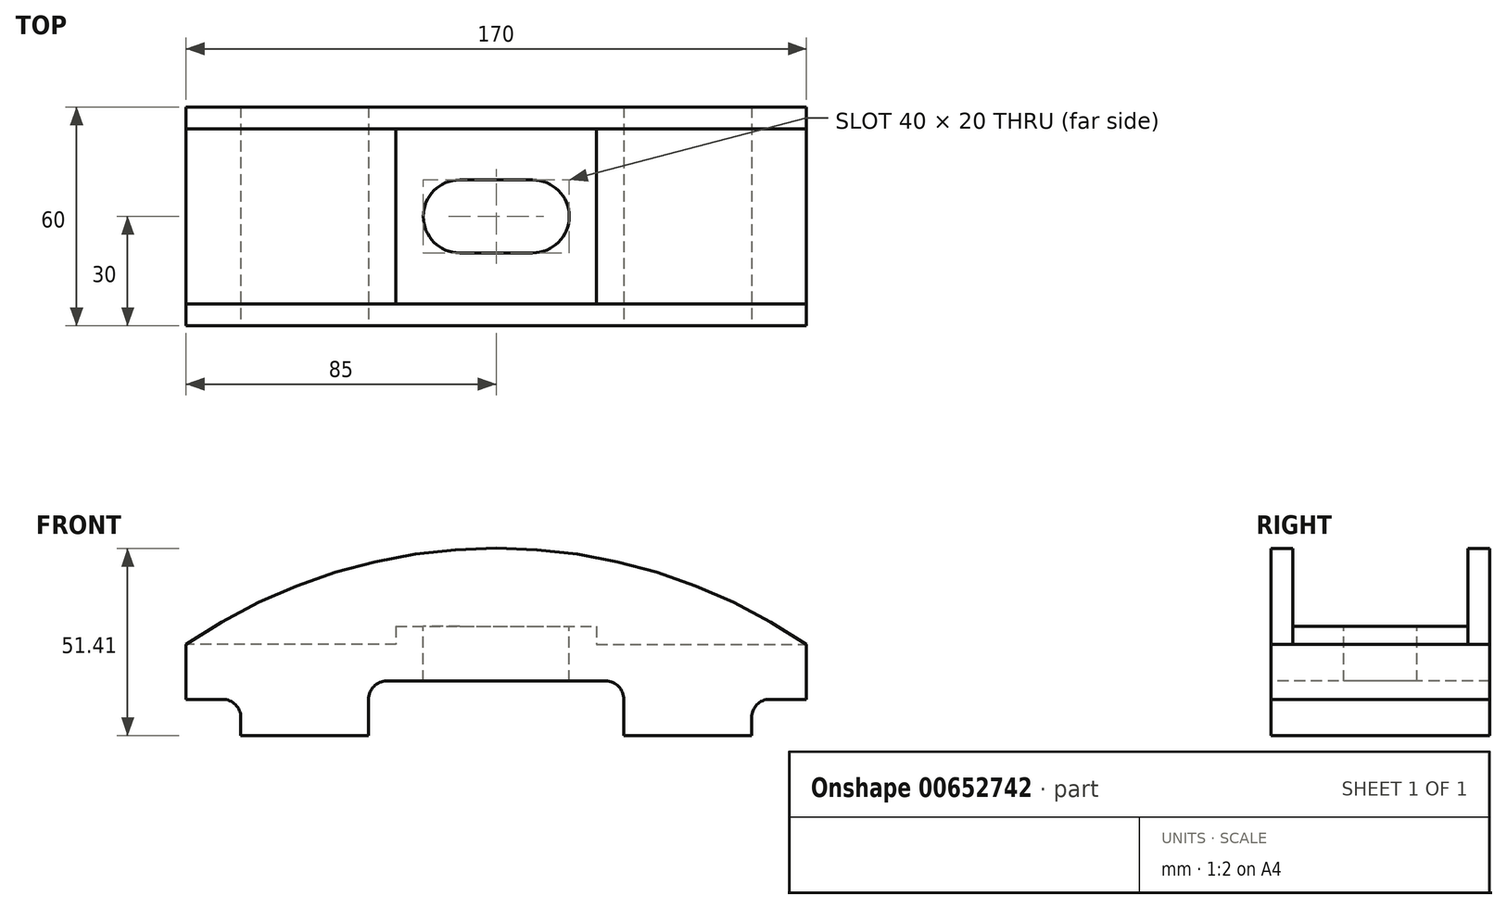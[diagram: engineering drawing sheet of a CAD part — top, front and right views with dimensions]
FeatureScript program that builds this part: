
annotation { "Feature Type Name" : "Feature", "Feature Type Description" : "" }
export const myFeature = defineFeature(function(context is Context, id is Id, definition is map)
    precondition{}
    {
        {
            var Q0;
            Q0=qCreatedBy(makeId("Front.planeOp"),FACE);
            var sketch = newSketch(context, id + "F0", { "sketchPlane" : qUnion([Q0])});
            skLineSegment(sketch, "E0.bottom", {"start": v(-85, 15) * mm, "end": v(85, 15) * mm});
            skLineSegment(sketch, "E0.top", {"start": v(-85, -15) * mm, "end": v(85, -15) * mm});
            skLineSegment(sketch, "E0.left", {"start": v(-85, 15) * mm, "end": v(-85, -15) * mm});
            skLineSegment(sketch, "E0.right", {"start": v(85, 15) * mm, "end": v(85, -15) * mm});
            skPoint(sketch, "E0.middle", {"position": v(0, 0) * mm});
            skSolve(sketch);
        }
        {
            var Q0;
            Q0 = qSketchRegion(id + "F0", true);
            extrude(context, id + "F1", {"entities" : qUnion([Q0]), "depth" : 60 * mm, "offsetDistance" : 25 * mm});
        }
        {
            var Q0;
            Q0=makeQuery(id+"F1.opExtrude","CAP_FACE",FACE,{"disambiguationData":[OSD([sQuery(id+"F0.wireOp",EDGE,"E0.bottom"),sQuery(id+"F0.wireOp",EDGE,"E0.top"),sQuery(id+"F0.wireOp",EDGE,"E0.left"),sQuery(id+"F0.wireOp",EDGE,"E0.right")])],"isStart":false});
            var sketch = newSketch(context, id + "F2", { "sketchPlane" : qUnion([Q0])});
            skPoint(sketch, "E1", {"position": v(0, -15) * mm});
            skPoint(sketch, "E2", {"position": v(35, -15) * mm});
            skPoint(sketch, "E3", {"position": v(-35, -15) * mm});
            skPoint(sketch, "E4", {"position": v(-35, 0) * mm});
            skPoint(sketch, "E5", {"position": v(35, 0) * mm});
            skLineSegment(sketch, "E6.bottom", {"start": v(-30, 0) * mm, "end": v(30, 0) * mm});
            skLineSegment(sketch, "E6.top", {"start": v(-35, -15) * mm, "end": v(35, -15) * mm});
            skLineSegment(sketch, "E6.left", {"start": v(-35, -5) * mm, "end": v(-35, -15) * mm});
            skLineSegment(sketch, "E6.right", {"start": v(35, -5) * mm, "end": v(35, -15) * mm});
            skArc(sketch, "E7.filletArc", {"start": v(-30, 0) * mm, "mid": v(-33.54, -1.46) * mm, "end": v(-35, -5) * mm});
            skArc(sketch, "E8.filletArc", {"start": v(35, -5) * mm, "mid": v(33.54, -1.46) * mm, "end": v(30, 0) * mm});
            skSolve(sketch);
        }
        {
            var Q0;
            Q0 = qSketchRegion(id + "F2", true);
            extrude(context, id + "F3", {"entities" : qUnion([Q0]), "operationType" : NewBodyOperationType.REMOVE, "endBound" : BoundingType.THROUGH_ALL, "oppositeDirection" : true, "depth" : 25 * mm, "offsetDistance" : 25 * mm});
        }
        {
            var Q0;
            Q0=makeQuery(id+"F1.opExtrude","CAP_FACE",FACE,{"disambiguationData":[OSD([sQuery(id+"F0.wireOp",EDGE,"E0.bottom"),sQuery(id+"F0.wireOp",EDGE,"E0.top"),sQuery(id+"F0.wireOp",EDGE,"E0.left"),sQuery(id+"F0.wireOp",EDGE,"E0.right")])],"isStart":false});
            var sketch = newSketch(context, id + "F4", { "sketchPlane" : qUnion([Q0])});
            skPoint(sketch, "E9", {"position": v(-70, -15) * mm});
            skLineSegment(sketch, "E10.bottom", {"start": v(-70, -15) * mm, "end": v(-85, -15) * mm});
            skLineSegment(sketch, "E10.top", {"start": v(-75, -5) * mm, "end": v(-85, -5) * mm});
            skLineSegment(sketch, "E10.left", {"start": v(-70, -15) * mm, "end": v(-70, -10) * mm});
            skLineSegment(sketch, "E10.right", {"start": v(-85, -15) * mm, "end": v(-85, -5) * mm});
            skPoint(sketch, "E11.visualSharp", {"position": v(-70, -5) * mm});
            skArc(sketch, "E11.filletArc", {"start": v(-70, -10) * mm, "mid": v(-71.46, -6.46) * mm, "end": v(-75, -5) * mm});
            skPoint(sketch, "E12", {"position": v(70, -15) * mm});
            skLineSegment(sketch, "E13.bottom", {"start": v(70, -15) * mm, "end": v(85, -15) * mm});
            skLineSegment(sketch, "E13.top", {"start": v(75, -5) * mm, "end": v(85, -5) * mm});
            skLineSegment(sketch, "E13.left", {"start": v(70, -15) * mm, "end": v(70, -10) * mm});
            skLineSegment(sketch, "E13.right", {"start": v(85, -15) * mm, "end": v(85, -5) * mm});
            skPoint(sketch, "E14.visualSharp", {"position": v(70, -5) * mm});
            skArc(sketch, "E14.filletArc", {"start": v(75, -5) * mm, "mid": v(71.46, -6.46) * mm, "end": v(70, -10) * mm});
            skSolve(sketch);
        }
        {
            var Q0;
            Q0 = qSketchRegion(id + "F4", true);
            extrude(context, id + "F5", {"entities" : qUnion([Q0]), "operationType" : NewBodyOperationType.REMOVE, "endBound" : BoundingType.THROUGH_ALL, "oppositeDirection" : true, "depth" : 25 * mm, "offsetDistance" : 25 * mm});
        }
        {
            var Q0;
            Q0=makeQuery(id+"F1.opExtrude","CAP_FACE",FACE,{"disambiguationData":[OSD([sQuery(id+"F0.wireOp",EDGE,"E0.bottom"),sQuery(id+"F0.wireOp",EDGE,"E0.top"),sQuery(id+"F0.wireOp",EDGE,"E0.left"),sQuery(id+"F0.wireOp",EDGE,"E0.right")])],"isStart":false});
            var sketch = newSketch(context, id + "F6", { "sketchPlane" : qUnion([Q0])});
            skPoint(sketch, "E15", {"position": v(27.5, 15) * mm});
            skPoint(sketch, "E16", {"position": v(-27.5, 15) * mm});
            skPoint(sketch, "E17", {"position": v(0, 15) * mm});
            skLineSegment(sketch, "E18.bottom", {"start": v(27.5, 15) * mm, "end": v(85, 15) * mm});
            skLineSegment(sketch, "E18.top", {"start": v(27.5, 10) * mm, "end": v(85, 10) * mm});
            skLineSegment(sketch, "E18.left", {"start": v(27.5, 15) * mm, "end": v(27.5, 10) * mm});
            skLineSegment(sketch, "E18.right", {"start": v(85, 15) * mm, "end": v(85, 10) * mm});
            skLineSegment(sketch, "E19.bottom", {"start": v(-27.5, 15) * mm, "end": v(-85, 15) * mm});
            skLineSegment(sketch, "E19.top", {"start": v(-27.5, 10) * mm, "end": v(-85, 10) * mm});
            skLineSegment(sketch, "E19.left", {"start": v(-27.5, 15) * mm, "end": v(-27.5, 10) * mm});
            skLineSegment(sketch, "E19.right", {"start": v(-85, 15) * mm, "end": v(-85, 10) * mm});
            skSolve(sketch);
        }
        {
            var Q0;
            Q0 = qSketchRegion(id + "F6", true);
            extrude(context, id + "F7", {"entities" : qUnion([Q0]), "operationType" : NewBodyOperationType.REMOVE, "endBound" : BoundingType.THROUGH_ALL, "oppositeDirection" : true, "depth" : 25 * mm, "offsetDistance" : 25 * mm});
        }
        {
            var Q0;
            Q0 = qSketchRegion(id + "F6", true);
            extrude(context, id + "F8", {"entities" : qUnion([Q0]), "operationType" : NewBodyOperationType.REMOVE, "endBound" : BoundingType.THROUGH_ALL, "oppositeDirection" : true, "depth" : 25 * mm, "offsetDistance" : 25 * mm});
        }
        {
            var Q0;
            Q0=makeQuery(id+"F1.opExtrude","CAP_FACE",FACE,{"disambiguationData":[OSD([sQuery(id+"F0.wireOp",EDGE,"E0.bottom"),sQuery(id+"F0.wireOp",EDGE,"E0.top"),sQuery(id+"F0.wireOp",EDGE,"E0.left"),sQuery(id+"F0.wireOp",EDGE,"E0.right")])],"isStart":false});
            var sketch = newSketch(context, id + "F9", { "sketchPlane" : qUnion([Q0])});
            skArc(sketch, "E20", {"start": v(85, 10) * mm, "mid": v(0, 36.4) * mm, "end": v(-85, 10) * mm});
            skLineSegment(sketch, "E21", {"start": v(-85, 10) * mm, "end": v(-27.5, 10) * mm});
            skLineSegment(sketch, "E22", {"start": v(-27.5, 10) * mm, "end": v(-27.5, 15) * mm});
            skLineSegment(sketch, "E23", {"start": v(-27.5, 15) * mm, "end": v(27.5, 15) * mm});
            skLineSegment(sketch, "E24", {"start": v(27.5, 15) * mm, "end": v(27.5, 10) * mm});
            skLineSegment(sketch, "E25", {"start": v(27.5, 10) * mm, "end": v(85, 10) * mm});
            skSolve(sketch);
        }
        {
            var Q0;
            Q0 = qSketchRegion(id + "F9", true);
            extrude(context, id + "F10", {"entities" : qUnion([Q0]), "operationType" : NewBodyOperationType.ADD, "oppositeDirection" : true, "depth" : 6 * mm, "offsetDistance" : 25 * mm});
        }
        {
            var Q0;
            Q0=makeQuery(id+"F1.opExtrude","CAP_FACE",FACE,{"disambiguationData":[OSD([sQuery(id+"F0.wireOp",EDGE,"E0.bottom"),sQuery(id+"F0.wireOp",EDGE,"E0.top"),sQuery(id+"F0.wireOp",EDGE,"E0.left"),sQuery(id+"F0.wireOp",EDGE,"E0.right")])],"isStart":true});
            var sketch = newSketch(context, id + "F11", { "sketchPlane" : qUnion([Q0])});
            skArc(sketch, "E26", {"start": v(85, 10) * mm, "mid": v(0, 36.4) * mm, "end": v(-85, 10) * mm});
            skLineSegment(sketch, "E27", {"start": v(-85, 10) * mm, "end": v(-27.5, 10) * mm});
            skLineSegment(sketch, "E28", {"start": v(-27.5, 10) * mm, "end": v(-27.5, 15) * mm});
            skLineSegment(sketch, "E29", {"start": v(-27.5, 15) * mm, "end": v(27.5, 15) * mm});
            skLineSegment(sketch, "E30", {"start": v(27.5, 15) * mm, "end": v(27.5, 10) * mm});
            skLineSegment(sketch, "E31", {"start": v(27.5, 10) * mm, "end": v(85, 10) * mm});
            skSolve(sketch);
        }
        {
            var Q0;
            Q0 = qSketchRegion(id + "F11", true);
            extrude(context, id + "F12", {"entities" : qUnion([Q0]), "operationType" : NewBodyOperationType.ADD, "oppositeDirection" : true, "depth" : 6 * mm, "offsetDistance" : 25 * mm});
        }
        {
            var Q0;
            Q0=makeQuery(id+"F1.opExtrude","SWEPT_FACE",FACE,{"disambiguationData":[OSD([sQuery(id+"F0.wireOp",EDGE,"E0.bottom")])]});
            var sketch = newSketch(context, id + "F13", { "sketchPlane" : qUnion([Q0])});
            skPoint(sketch, "E32", {"position": v(0, -6) * mm});
            skPoint(sketch, "E33", {"position": v(0, -54) * mm});
            skPoint(sketch, "E34", {"position": v(0, -30) * mm});
            skLineSegment(sketch, "E35.bottom", {"start": v(-10, -20) * mm, "end": v(10, -20) * mm});
            skLineSegment(sketch, "E35.top", {"start": v(-10, -40) * mm, "end": v(10, -40) * mm});
            skArc(sketch, "E36", {"start": v(-10, -20) * mm, "mid": v(-20, -30) * mm, "end": v(-10, -40) * mm});
            skArc(sketch, "E37", {"start": v(10, -40) * mm, "mid": v(20, -30) * mm, "end": v(10, -20) * mm});
            skSolve(sketch);
        }
        {
            var Q0;
            Q0 = qSketchRegion(id + "F13", true);
            extrude(context, id + "F14", {"entities" : qUnion([Q0]), "operationType" : NewBodyOperationType.REMOVE, "endBound" : BoundingType.THROUGH_ALL, "oppositeDirection" : true, "depth" : 25 * mm, "offsetDistance" : 25 * mm});
        }
    });
